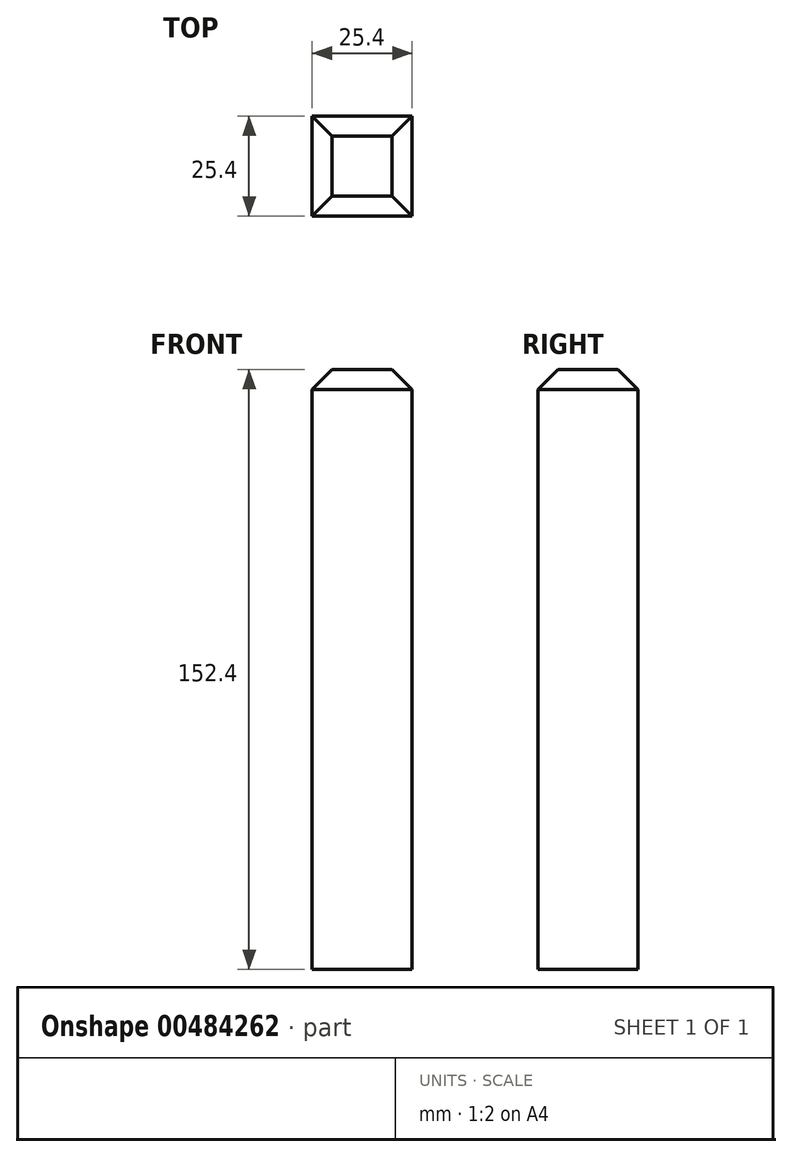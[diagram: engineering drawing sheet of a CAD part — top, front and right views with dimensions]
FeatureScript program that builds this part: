
annotation { "Feature Type Name" : "Feature", "Feature Type Description" : "" }
export const myFeature = defineFeature(function(context is Context, id is Id, definition is map)
    precondition{}
    {
        {
            var Q0;
            Q0=qCreatedBy(makeId("Top.planeOp"),FACE);
            var sketch = newSketch(context, id + "F0", { "sketchPlane" : qUnion([Q0])});
            skLineSegment(sketch, "E0.bottom", {"start": v(12.7, 12.7) * mm, "end": v(-12.7, 12.7) * mm});
            skLineSegment(sketch, "E0.top", {"start": v(12.7, -12.7) * mm, "end": v(-12.7, -12.7) * mm});
            skLineSegment(sketch, "E0.left", {"start": v(12.7, 12.7) * mm, "end": v(12.7, -12.7) * mm});
            skLineSegment(sketch, "E0.right", {"start": v(-12.7, 12.7) * mm, "end": v(-12.7, -12.7) * mm});
            skPoint(sketch, "E0.middle", {"position": v(0, 0) * mm});
            skSolve(sketch);
        }
        {
            var Q0;
            Q0=makeQuery(id+"F0.imprint","IMPRINT",FACE,{"disambiguationData":[TD([[makeQuery(id+"F0.imprint","IMPRINT",EDGE,{"derivedFrom":sQuery(id+"F0.wireOp",EDGE,"E0.bottom")}),1.0]])]});
            extrude(context, id + "F1", {"entities" : qUnion([Q0]), "depth" : 152.4 * mm});
        }
        {
            var Q0;
            Q0=makeQuery(id+"F1.opExtrude","CAP_EDGE",EDGE,{"disambiguationData":[OSD([sQuery(id+"F0.wireOp",EDGE,"E0.right")])],"isStart":false});
            var Q1;
            Q1=makeQuery(id+"F1.opExtrude","CAP_EDGE",EDGE,{"disambiguationData":[OSD([sQuery(id+"F0.wireOp",EDGE,"E0.bottom")])],"isStart":false});
            var Q2;
            Q2=makeQuery(id+"F1.opExtrude","CAP_EDGE",EDGE,{"disambiguationData":[OSD([sQuery(id+"F0.wireOp",EDGE,"E0.left")])],"isStart":false});
            var Q3;
            Q3=makeQuery(id+"F1.opExtrude","CAP_EDGE",EDGE,{"disambiguationData":[OSD([sQuery(id+"F0.wireOp",EDGE,"E0.top")])],"isStart":false});
            chamfer(context, id + "F2", {"entities" : qUnion([Q0, Q1, Q2, Q3]), "width" : 5.08 * mm, "tangentPropagation" : true});
        }
    });
